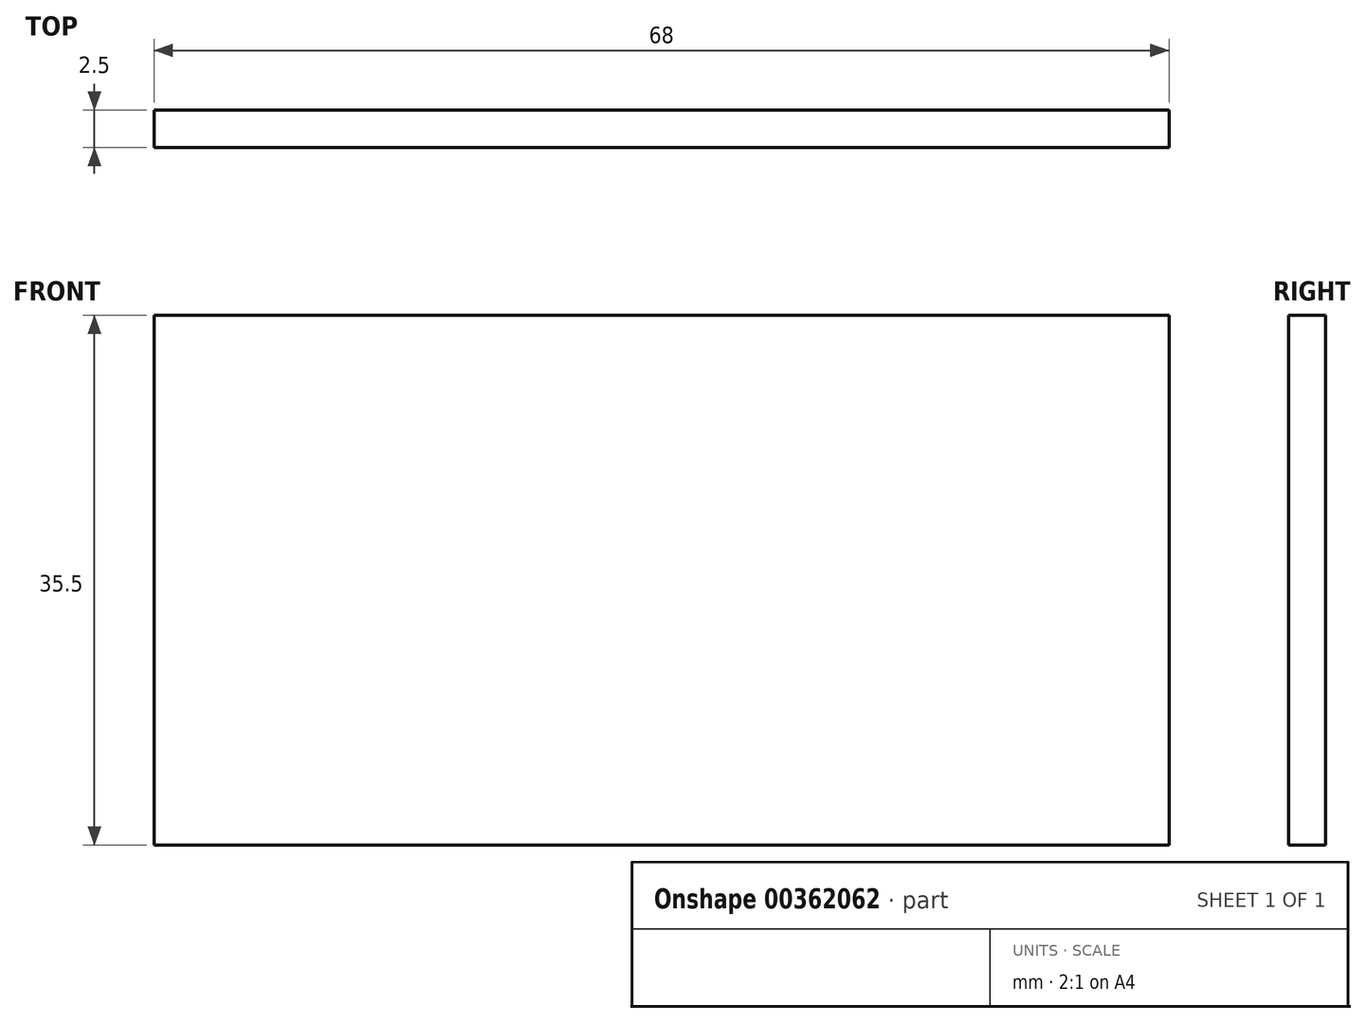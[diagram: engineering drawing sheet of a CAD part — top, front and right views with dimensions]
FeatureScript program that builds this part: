
annotation { "Feature Type Name" : "Feature", "Feature Type Description" : "" }
export const myFeature = defineFeature(function(context is Context, id is Id, definition is map)
    precondition{}
    {
        {
            var Q0;
            Q0=qCreatedBy(makeId("Front.planeOp"),FACE);
            var sketch = newSketch(context, id + "F0", { "sketchPlane" : qUnion([Q0])});
            skLineSegment(sketch, "E0", {"start": v(0, 0) * mm, "end": v(0, 35.5) * mm});
            skLineSegment(sketch, "E1", {"start": v(0, 35.5) * mm, "end": v(68, 35.5) * mm});
            skLineSegment(sketch, "E2", {"start": v(68, 35.5) * mm, "end": v(68, 0) * mm});
            skLineSegment(sketch, "E3", {"start": v(68, 0) * mm, "end": v(0, 0) * mm});
            skSolve(sketch);
        }
        {
            var Q0;
            Q0=qSketchRegion(id+"F0",true);
            extrude(context, id + "F1", {"entities" : qUnion([Q0]), "depth" : 2.5 * mm});
        }
    });
